# Revit family: Grinder_Pumps-Progressing_Cavity-Zoeller-Sewage_Waste-7021_Series
name_source: partatom
category: Mechanical Equipment
revit_build: Autodesk Revit 2014 (Build: 20130308_1515(x64)
units: mm (PartAtom-declared; Revit-internal decimal feet)

## types (2) — shared parameters
Cooling = Oil filled
Cord Length = 240"
Cord Type = SOW or SOOW, multi-wire neoprene
Default Elevation = 0"
Description = Shark® Series. 7020, 7021 Grinder Pumps. Progressing cavity grinder pumps.
Discharge Radius = 5/8"
Discharge Size = 1 1/4" NPT Horizontal
Height = 22 3/8"
Hertz = 60
Installation Type = Floor Mounted
Insulation = Class B
Length = 8"
Manufacturer = Zoeller
Material = Cast Iron-Zoeller-Powder Coated Epoxy
Max Flow Rate = 14.6 GPM (55.3 LPM)
Max. Operating Temp. = 54°C (130°F)
Mechanical Seals = Carbon/ceramic
Motor Protection = Auto reset thermal overload
Operation = Non-Automatic
Phase = 1 Ph
Price = Prices may vary. Please consult Manufacturer Representative for most up-to-date price list.
Product Page URL = http://www.zoellerengprod.com
RPM = 1750
Type = Permanent Split Capacitor
URL = http://www.zoellerpumps.com
Voltage = 230 V
Warranty Information = 36 Months (Limited)
Waste Connection = Yes
Width = 8 3/8"

## per-type parameters (varying)
| type | Amps | Apparent Load | Maximum Head | Model | Motor |
| E7020 | 7 A | 1610 VA | 150' (45.7 m) | 7020 | 1 HP |
| E7021 | 11 A | 2415 VA | 240' (73.2 m) | 7021 | 2 HP |

## geometry (parser evidence)
native form markers: Sweep x1
no freeform markers — native parametric forms only
